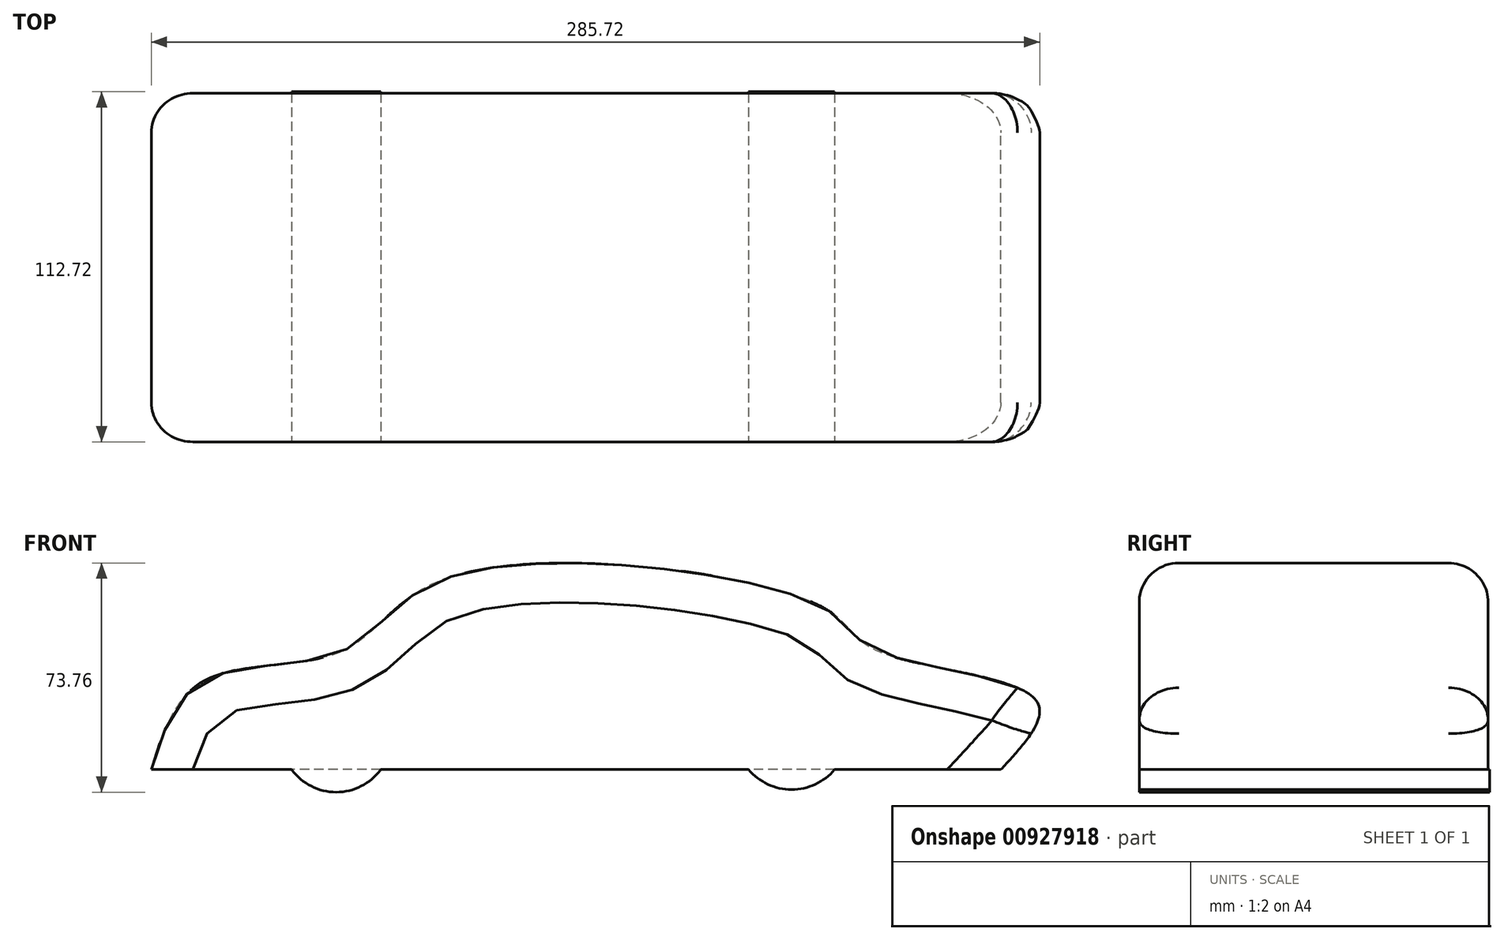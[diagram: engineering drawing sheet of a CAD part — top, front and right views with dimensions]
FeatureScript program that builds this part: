
annotation { "Feature Type Name" : "Feature", "Feature Type Description" : "" }
export const myFeature = defineFeature(function(context is Context, id is Id, definition is map)
    precondition{}
    {
        {
            var Q0;
            Q0=qCreatedBy(makeId("Front.planeOp"),FACE);
            var sketch = newSketch(context, id + "F0", { "sketchPlane" : qUnion([Q0])});
            skFitSpline(sketch, "E0", {"points": [v(-118.8, 0) * mm, v(-101.58, 28.73) * mm, v(-57.65, 38.01) * mm, v(-22.83, 61.95) * mm, v(97.06, 52.3) * mm, v(114.32, 38.34) * mm, v(165.69, 22.36) * mm, v(154.4, 0) * mm], "startDerivative": vector(88.32, 285) * mm, "endDerivative": vector(-219.68, -236.86) * mm});
            skLineSegment(sketch, "E1", {"start": v(154.4, 0) * mm, "end": v(-118.8, 0) * mm});
            skSolve(sketch);
        }
        {
            var Q0;
            Q0=makeQuery(id+"F0.imprint","IMPRINT",FACE,{"disambiguationData":[TD([[makeQuery(id+"F0.imprint","IMPRINT",EDGE,{"derivedFrom":sQuery(id+"F0.wireOp",EDGE,"E0")}),-1.0]])]});
            extrude(context, id + "F1", {"entities" : qUnion([Q0]), "depth" : 112.24 * mm, "offsetDistance" : 25.4 * mm});
        }
        {
            var Q0;
            Q0=makeQuery(id+"F1.opExtrude","CAP_EDGE",EDGE,{"disambiguationData":[OSD([sQuery(id+"F0.wireOp",EDGE,"E0")])],"isStart":false});
            var Q1;
            Q1=makeQuery(id+"F1.opExtrude","CAP_EDGE",EDGE,{"disambiguationData":[OSD([sQuery(id+"F0.wireOp",EDGE,"E0")])],"isStart":true});
            fillet(context, id + "F2", {"entities" : qUnion([Q0, Q1]), "radius" : 12.7 * mm, "tangentPropagation" : true, "allowEdgeOverflow" : false});
        }
        {
            var Q0;
            Q0=makeQuery(id+"F1.opExtrude","CAP_FACE",FACE,{"disambiguationData":[OSD([sQuery(id+"F0.wireOp",EDGE,"E0"),sQuery(id+"F0.wireOp",EDGE,"E1")])],"isStart":false});
            var sketch = newSketch(context, id + "F3", { "sketchPlane" : qUnion([Q0])});
            skArc(sketch, "E2", {"start": v(-73.68, 0) * mm, "mid": v(-59.35, -7.26) * mm, "end": v(-45.01, 0) * mm});
            skArc(sketch, "E3", {"start": v(73.26, 0) * mm, "mid": v(87.12, -6.4) * mm, "end": v(100.98, 0) * mm});
            skLineSegment(sketch, "E4.0", {"start": v(100.98, 0) * mm, "end": v(73.26, 0) * mm});
            skLineSegment(sketch, "E5.trimOffspring", {"start": v(-45.01, 0) * mm, "end": v(-73.68, 0) * mm});
            skPoint(sketch, "E6.orphan", {"position": v(-105.49, 0) * mm});
            skPoint(sketch, "E7.orphan", {"position": v(137.08, 0) * mm});
            skSolve(sketch);
        }
        {
            var Q0;
            Q0 = qSketchRegion(id + "F3", true);
            extrude(context, id + "F4", {"entities" : qUnion([Q0]), "operationType" : NewBodyOperationType.ADD, "oppositeDirection" : true, "depth" : 112.7 * mm, "offsetDistance" : 25.4 * mm});
        }
    });
